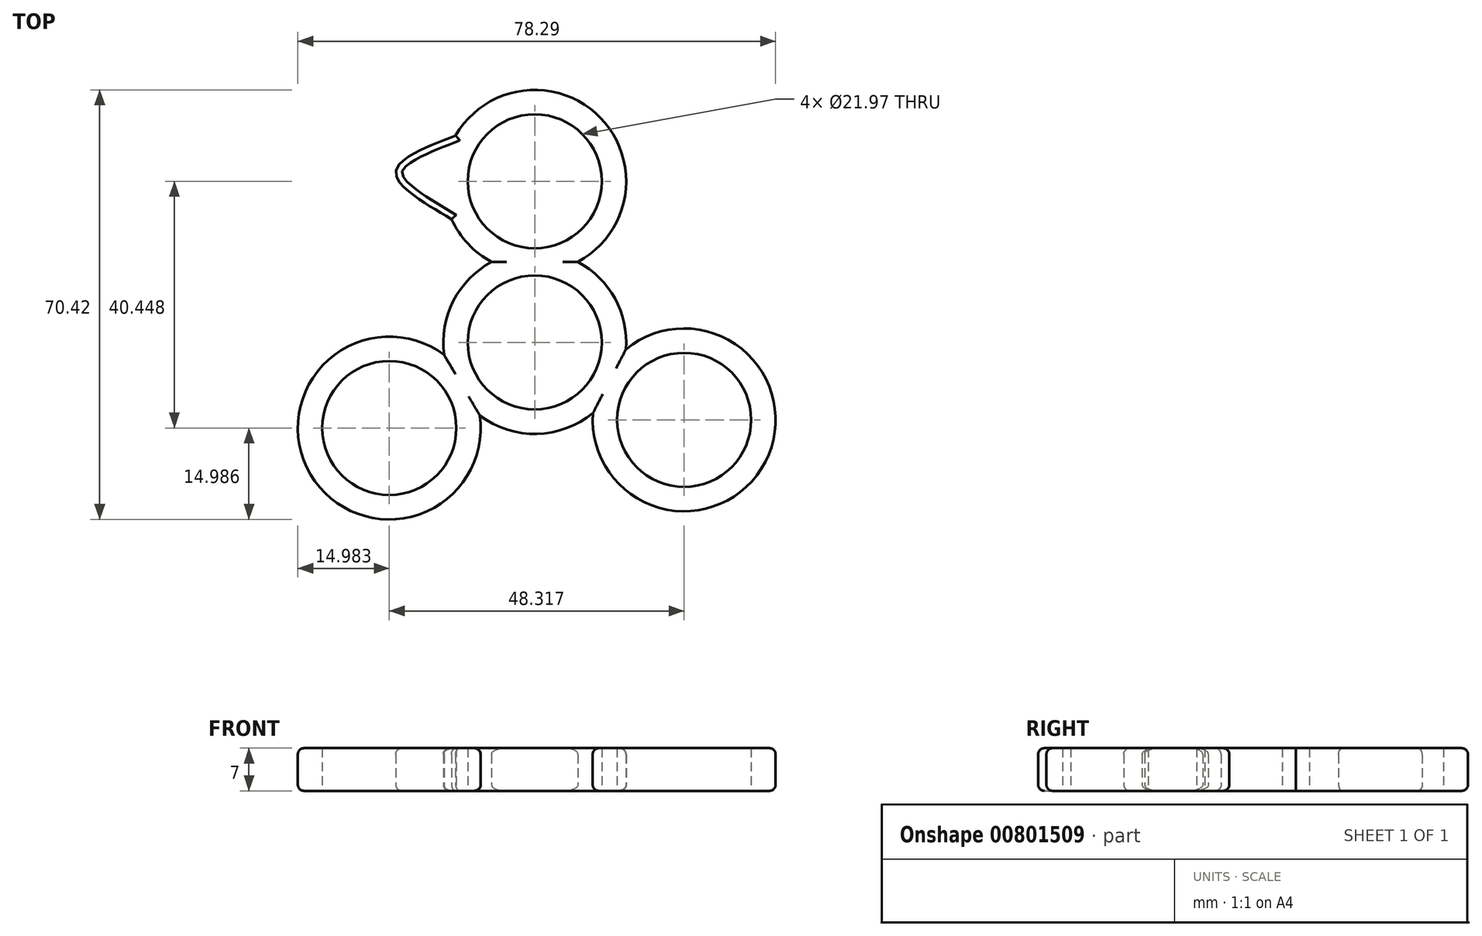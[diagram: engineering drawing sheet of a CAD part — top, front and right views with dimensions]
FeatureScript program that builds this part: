
annotation { "Feature Type Name" : "Feature", "Feature Type Description" : "" }
export const myFeature = defineFeature(function(context is Context, id is Id, definition is map)
    precondition{}
    {
        {
            var Q0;
            Q0=qCreatedBy(makeId("Top.planeOp"),FACE);
            var sketch = newSketch(context, id + "F0", { "sketchPlane" : qUnion([Q0])});
            skCircle(sketch, "E0", {"center": v(0, 0) * mm, "radius": 10.99 * mm});
            skCircle(sketch, "E1", {"center": v(0, 26.42) * mm, "radius": 10.99 * mm});
            skCircle(sketch, "E2", {"center": v(24.48, -12.68) * mm, "radius": 10.99 * mm});
            skCircle(sketch, "E3", {"center": v(-23.84, -14.02) * mm, "radius": 10.99 * mm});
            skArc(sketch, "E4", {"start": v(7.07, 13.21) * mm, "mid": v(10.77, 36.84) * mm, "end": v(-12.97, 33.93) * mm});
            skArc(sketch, "E5", {"start": v(-7.07, 13.21) * mm, "mid": v(-13.35, 6.8) * mm, "end": v(-14.85, -2.03) * mm});
            skArc(sketch, "E6", {"start": v(9.54, -11.56) * mm, "mid": v(37.79, -19.58) * mm, "end": v(14.94, -1.12) * mm});
            skArc(sketch, "E7", {"start": v(-14.85, -2.03) * mm, "mid": v(-36.75, -21.62) * mm, "end": v(-8.99, -12) * mm});
            skArc(sketch, "E8.trimOffspring", {"start": v(14.94, -1.12) * mm, "mid": v(13.14, 7.21) * mm, "end": v(7.07, 13.21) * mm});
            skArc(sketch, "E9.trimOffspring", {"start": v(-8.99, -12) * mm, "mid": v(0.35, -14.98) * mm, "end": v(9.54, -11.56) * mm});
            skFitSpline(sketch, "E10", {"points": [v(-12.97, 33.93) * mm, v(-22.77, 27.98) * mm, v(-13.64, 20.22) * mm], "startDerivative": vector(-29.05, -11.29) * mm, "endDerivative": vector(27.56, -16.2) * mm});
            skArc(sketch, "E11.trimOffspring", {"start": v(-13.64, 20.22) * mm, "mid": v(-10.93, 16.17) * mm, "end": v(-7.07, 13.21) * mm});
            skSolve(sketch);
        }
        {
            var Q0;
            Q0=makeQuery(id+"F0.imprint","IMPRINT",FACE,{"disambiguationData":[TD([[makeQuery(id+"F0.imprint","IMPRINT",EDGE,{"derivedFrom":sQuery(id+"F0.wireOp",EDGE,"E0")}),-1.0]])]});
            extrude(context, id + "F1", {"entities" : qUnion([Q0]), "depth" : 7 * mm, "offsetDistance" : 25.4 * mm});
        }
        {
            var Q0;
            Q0=makeQuery(id+"F1.opExtrude","CAP_EDGE",EDGE,{"disambiguationData":[OSD([sQuery(id+"F0.wireOp",EDGE,"E4")])],"isStart":false});
            var Q1;
            Q1=makeQuery(id+"F1.opExtrude","CAP_EDGE",EDGE,{"disambiguationData":[OSD([sQuery(id+"F0.wireOp",EDGE,"E10")])],"isStart":false});
            var Q2;
            Q2=makeQuery(id+"F1.opExtrude","CAP_EDGE",EDGE,{"disambiguationData":[OSD([sQuery(id+"F0.wireOp",EDGE,"E11.trimOffspring")])],"isStart":false});
            var Q3;
            Q3=makeQuery(id+"F1.opExtrude","CAP_EDGE",EDGE,{"disambiguationData":[OSD([sQuery(id+"F0.wireOp",EDGE,"E5")])],"isStart":false});
            var Q4;
            Q4=makeQuery(id+"F1.opExtrude","CAP_EDGE",EDGE,{"disambiguationData":[OSD([sQuery(id+"F0.wireOp",EDGE,"E7")])],"isStart":false});
            var Q5;
            Q5=makeQuery(id+"F1.opExtrude","CAP_EDGE",EDGE,{"disambiguationData":[OSD([sQuery(id+"F0.wireOp",EDGE,"E9.trimOffspring")])],"isStart":false});
            var Q6;
            Q6=makeQuery(id+"F1.opExtrude","CAP_EDGE",EDGE,{"disambiguationData":[OSD([sQuery(id+"F0.wireOp",EDGE,"E6")])],"isStart":false});
            var Q7;
            Q7=makeQuery(id+"F1.opExtrude","CAP_EDGE",EDGE,{"disambiguationData":[OSD([sQuery(id+"F0.wireOp",EDGE,"E8.trimOffspring")])],"isStart":false});
            fillet(context, id + "F2", {"entities" : qUnion([Q0, Q1, Q2, Q3, Q4, Q5, Q6, Q7]), "radius" : 1 * mm, "tangentPropagation" : true, "allowEdgeOverflow" : false});
        }
        {
            var Q0;
            Q0=makeQuery(id+"F1.opExtrude","CAP_EDGE",EDGE,{"disambiguationData":[OSD([sQuery(id+"F0.wireOp",EDGE,"E4")])],"isStart":true});
            var Q1;
            Q1=makeQuery(id+"F1.opExtrude","CAP_EDGE",EDGE,{"disambiguationData":[OSD([sQuery(id+"F0.wireOp",EDGE,"E10")])],"isStart":true});
            fillet(context, id + "F3", {"entities" : qUnion([Q0, Q1]), "radius" : 1 * mm, "tangentPropagation" : true, "allowEdgeOverflow" : false});
        }
        {
            var Q0;
            Q0=makeQuery(id+"F1.opExtrude","CAP_EDGE",EDGE,{"disambiguationData":[OSD([sQuery(id+"F0.wireOp",EDGE,"E6")])],"isStart":true});
            var Q1;
            Q1=makeQuery(id+"F1.opExtrude","CAP_EDGE",EDGE,{"disambiguationData":[OSD([sQuery(id+"F0.wireOp",EDGE,"E9.trimOffspring")])],"isStart":true});
            var Q2;
            Q2=makeQuery(id+"F1.opExtrude","CAP_EDGE",EDGE,{"disambiguationData":[OSD([sQuery(id+"F0.wireOp",EDGE,"E7")])],"isStart":true});
            var Q3;
            Q3=makeQuery(id+"F1.opExtrude","CAP_EDGE",EDGE,{"disambiguationData":[OSD([sQuery(id+"F0.wireOp",EDGE,"E5")])],"isStart":true});
            var Q4;
            Q4=makeQuery(id+"F1.opExtrude","CAP_EDGE",EDGE,{"disambiguationData":[OSD([sQuery(id+"F0.wireOp",EDGE,"E11.trimOffspring")])],"isStart":true});
            var Q5;
            Q5=makeQuery(id+"F1.opExtrude","CAP_EDGE",EDGE,{"disambiguationData":[OSD([sQuery(id+"F0.wireOp",EDGE,"E8.trimOffspring")])],"isStart":true});
            fillet(context, id + "F4", {"entities" : qUnion([Q0, Q1, Q2, Q3, Q4, Q5]), "radius" : 1 * mm, "tangentPropagation" : true, "allowEdgeOverflow" : false});
        }
    });
